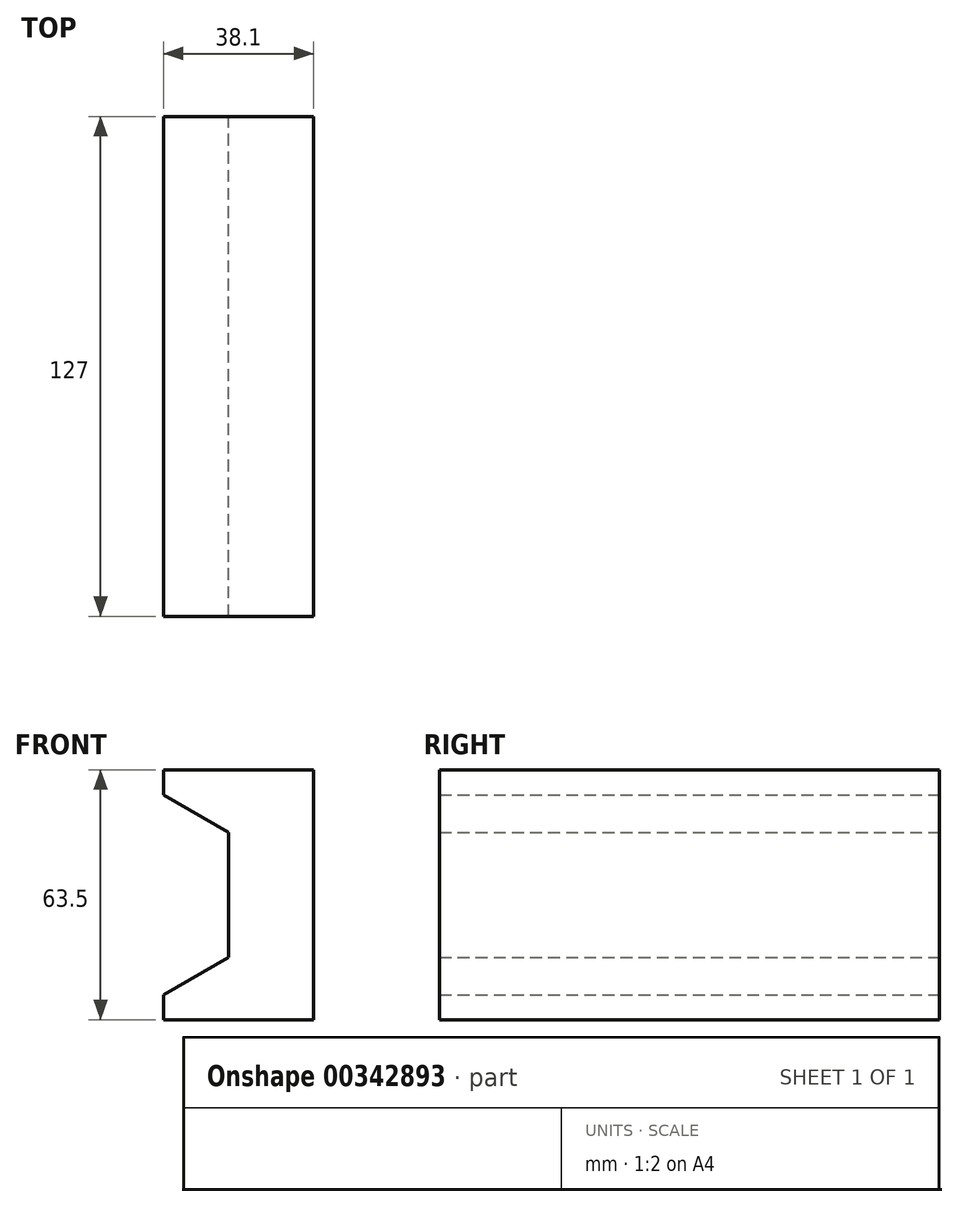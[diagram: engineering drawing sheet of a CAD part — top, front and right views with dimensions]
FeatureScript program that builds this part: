
annotation { "Feature Type Name" : "Feature", "Feature Type Description" : "" }
export const myFeature = defineFeature(function(context is Context, id is Id, definition is map)
    precondition{}
    {
        {
            var Q0;
            Q0=qCreatedBy(makeId("Front.planeOp"),FACE);
            var sketch = newSketch(context, id + "F0", { "sketchPlane" : qUnion([Q0])});
            skLineSegment(sketch, "E0", {"start": v(19.58, 28.64) * mm, "end": v(19.58, -34.86) * mm});
            skLineSegment(sketch, "E1", {"start": v(19.58, -34.86) * mm, "end": v(-18.52, -34.86) * mm});
            skLineSegment(sketch, "E2", {"start": v(19.58, 28.64) * mm, "end": v(-18.52, 28.64) * mm});
            skLineSegment(sketch, "E3", {"start": v(-18.52, -34.86) * mm, "end": v(-18.52, -28.5) * mm});
            skLineSegment(sketch, "E4", {"start": v(-18.52, 28.64) * mm, "end": v(-18.52, 22.3) * mm});
            skLineSegment(sketch, "E5", {"start": v(-18.52, 22.3) * mm, "end": v(-2.02, 12.77) * mm});
            skLineSegment(sketch, "E6", {"start": v(-18.52, -28.5) * mm, "end": v(-2.02, -18.98) * mm});
            skLineSegment(sketch, "E7", {"start": v(-2.02, 12.77) * mm, "end": v(-2.02, -18.98) * mm});
            skPoint(sketch, "E8.end.orphan", {"position": v(0, -28.5) * mm});
            skSolve(sketch);
        }
        {
            var Q0;
            Q0=makeQuery(id+"F0.imprint","IMPRINT",FACE,{"disambiguationData":[TD([[makeQuery(id+"F0.imprint","IMPRINT",EDGE,{"derivedFrom":sQuery(id+"F0.wireOp",EDGE,"E0")}),-1.0]])]});
            extrude(context, id + "F1", {"entities" : qUnion([Q0]), "depth" : 127 * mm});
        }
    });
